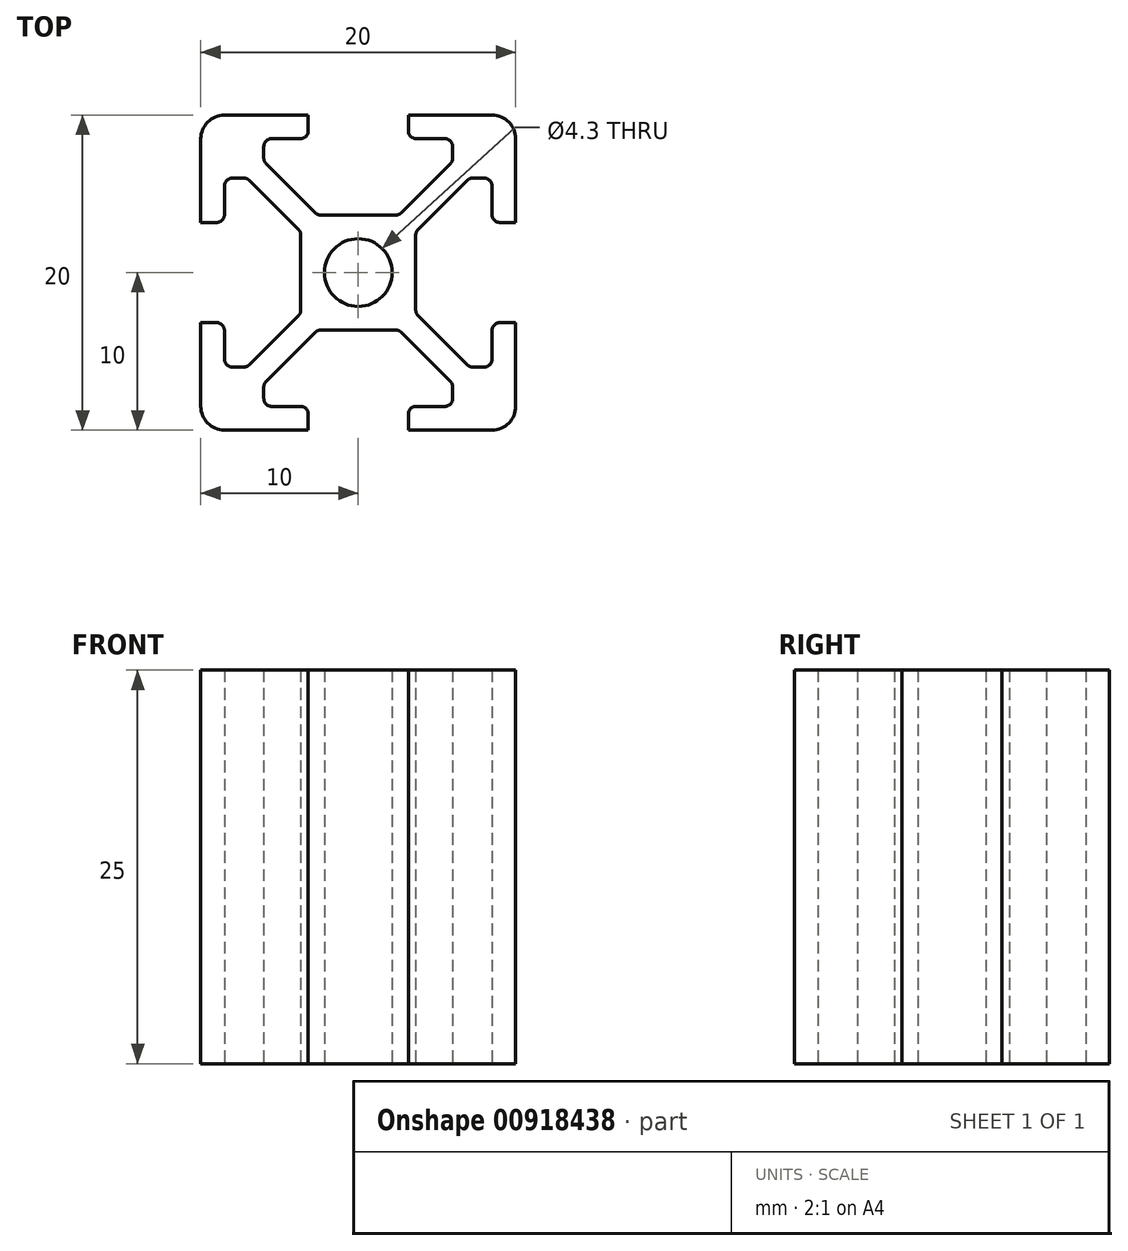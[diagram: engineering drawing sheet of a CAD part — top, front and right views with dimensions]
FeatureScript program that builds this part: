
annotation { "Feature Type Name" : "Feature", "Feature Type Description" : "" }
export const myFeature = defineFeature(function(context is Context, id is Id, definition is map)
    precondition{}
    {
        {
            var Q0;
            Q0=qCreatedBy(makeId("Top.planeOp"),FACE);
            var sketch = newSketch(context, id + "F0", { "sketchPlane" : qUnion([Q0])});
            skPoint(sketch, "E0.middle", {"position": v(0, 0) * mm});
            skCircle(sketch, "E1", {"center": v(0, 0) * mm, "radius": 2.15 * mm});
            skLineSegment(sketch, "E2.bottom", {"start": v(10, 10) * mm, "end": v(-10, 10) * mm});
            skLineSegment(sketch, "E2.top", {"start": v(10, -10) * mm, "end": v(-10, -10) * mm});
            skLineSegment(sketch, "E2.left", {"start": v(10, 10) * mm, "end": v(10, -10) * mm});
            skLineSegment(sketch, "E2.right", {"start": v(-10, 10) * mm, "end": v(-10, -10) * mm});
            skSolve(sketch);
        }
        {
            var Q0;
            Q0=makeQuery(id+"F0.imprint","IMPRINT",FACE,{"disambiguationData":[TD([[makeQuery(id+"F0.imprint","IMPRINT",EDGE,{"derivedFrom":sQuery(id+"F0.wireOp",EDGE,"E1")}),-1.0]])]});
            var sketch = newSketch(context, id + "F1", { "sketchPlane" : qUnion([Q0])});
            skLineSegment(sketch, "E3", {"start": v(-3.18, 10) * mm, "end": v(3.18, 10) * mm});
            skLineSegment(sketch, "E4", {"start": v(3.18, 10) * mm, "end": v(3.18, 8.5) * mm});
            skLineSegment(sketch, "E5", {"start": v(3.18, 8.5) * mm, "end": v(6, 8.5) * mm});
            skLineSegment(sketch, "E6", {"start": v(6, 8.5) * mm, "end": v(6, 7.06) * mm});
            skLineSegment(sketch, "E7", {"start": v(6, 7.06) * mm, "end": v(2.59, 3.65) * mm});
            skLineSegment(sketch, "E8", {"start": v(2.59, 3.65) * mm, "end": v(-2.59, 3.65) * mm});
            skLineSegment(sketch, "E9", {"start": v(-2.59, 3.65) * mm, "end": v(-6, 7.06) * mm});
            skLineSegment(sketch, "E10", {"start": v(-6, 7.06) * mm, "end": v(-6, 8.5) * mm});
            skLineSegment(sketch, "E11", {"start": v(-6, 8.5) * mm, "end": v(-3.18, 8.5) * mm});
            skLineSegment(sketch, "E12", {"start": v(-3.18, 8.5) * mm, "end": v(-3.18, 10) * mm});
            skPoint(sketch, "E13", {"position": v(0, 10) * mm});
            skPoint(sketch, "E14", {"position": v(0, 3.65) * mm});
            skPoint(sketch, "E15.center", {"position": v(0.01, -0.04) * mm});
            skLineSegment(sketch, "E16.0.0", {"start": v(-10, -10) * mm, "end": v(10, -10) * mm});
            skLineSegment(sketch, "E16.0.1", {"start": v(10, -10) * mm, "end": v(10, 10) * mm});
            skLineSegment(sketch, "E16.0.2", {"start": v(10, 10) * mm, "end": v(-10, 10) * mm});
            skLineSegment(sketch, "E16.0.3", {"start": v(-10, 10) * mm, "end": v(-10, -10) * mm});
            skLineSegment(sketch, "E17", {"start": v(0, 0) * mm, "end": v(10, 10) * mm, "construction": true});
            skLineSegment(sketch, "E18.1.0", {"start": v(-8.5, -3.18) * mm, "end": v(-10, -3.18) * mm});
            skLineSegment(sketch, "E18.1.1", {"start": v(-8.5, -6) * mm, "end": v(-8.5, -3.18) * mm});
            skLineSegment(sketch, "E18.1.2", {"start": v(-7.06, -6) * mm, "end": v(-8.5, -6) * mm});
            skLineSegment(sketch, "E18.1.3", {"start": v(-3.65, -2.59) * mm, "end": v(-7.06, -6) * mm});
            skLineSegment(sketch, "E18.1.4", {"start": v(-3.65, 2.59) * mm, "end": v(-3.65, -2.59) * mm});
            skLineSegment(sketch, "E18.1.5", {"start": v(-7.06, 6) * mm, "end": v(-3.65, 2.59) * mm});
            skLineSegment(sketch, "E18.1.6", {"start": v(-8.5, 6) * mm, "end": v(-7.06, 6) * mm});
            skLineSegment(sketch, "E18.1.7", {"start": v(-8.5, 3.18) * mm, "end": v(-8.5, 6) * mm});
            skLineSegment(sketch, "E18.1.8", {"start": v(-10, 3.18) * mm, "end": v(-8.5, 3.18) * mm});
            skLineSegment(sketch, "E18.2.0", {"start": v(3.18, -8.5) * mm, "end": v(3.18, -10) * mm});
            skLineSegment(sketch, "E18.2.1", {"start": v(6, -8.5) * mm, "end": v(3.18, -8.5) * mm});
            skLineSegment(sketch, "E18.2.2", {"start": v(6, -7.06) * mm, "end": v(6, -8.5) * mm});
            skLineSegment(sketch, "E18.2.3", {"start": v(2.59, -3.65) * mm, "end": v(6, -7.06) * mm});
            skLineSegment(sketch, "E18.2.4", {"start": v(-2.59, -3.65) * mm, "end": v(2.59, -3.65) * mm});
            skLineSegment(sketch, "E18.2.5", {"start": v(-6, -7.06) * mm, "end": v(-2.59, -3.65) * mm});
            skLineSegment(sketch, "E18.2.6", {"start": v(-6, -8.5) * mm, "end": v(-6, -7.06) * mm});
            skLineSegment(sketch, "E18.2.7", {"start": v(-3.18, -8.5) * mm, "end": v(-6, -8.5) * mm});
            skLineSegment(sketch, "E18.2.8", {"start": v(-3.18, -10) * mm, "end": v(-3.18, -8.5) * mm});
            skLineSegment(sketch, "E18.3.0", {"start": v(8.5, 3.18) * mm, "end": v(10, 3.18) * mm});
            skLineSegment(sketch, "E18.3.1", {"start": v(8.5, 6) * mm, "end": v(8.5, 3.18) * mm});
            skLineSegment(sketch, "E18.3.2", {"start": v(7.06, 6) * mm, "end": v(8.5, 6) * mm});
            skLineSegment(sketch, "E18.3.3", {"start": v(3.65, 2.59) * mm, "end": v(7.06, 6) * mm});
            skLineSegment(sketch, "E18.3.4", {"start": v(3.65, -2.59) * mm, "end": v(3.65, 2.59) * mm});
            skLineSegment(sketch, "E18.3.5", {"start": v(7.06, -6) * mm, "end": v(3.65, -2.59) * mm});
            skLineSegment(sketch, "E18.3.6", {"start": v(8.5, -6) * mm, "end": v(7.06, -6) * mm});
            skLineSegment(sketch, "E18.3.7", {"start": v(8.5, -3.18) * mm, "end": v(8.5, -6) * mm});
            skLineSegment(sketch, "E18.3.8", {"start": v(10, -3.18) * mm, "end": v(8.5, -3.18) * mm});
            skPoint(sketch, "E18.center", {"position": v(0, 0) * mm});
            skSolve(sketch);
        }
        {
            var Q0;
            Q0=makeQuery(id+"F0.imprint","IMPRINT",FACE,{"disambiguationData":[TD([[makeQuery(id+"F0.imprint","IMPRINT",EDGE,{"derivedFrom":sQuery(id+"F0.wireOp",EDGE,"E1")}),-1.0]])]});
            extrude(context, id + "F2", {"entities" : qUnion([Q0]), "flatOperationType" : FlatOperationType.REMOVE, "depth" : 25 * mm, "offsetDistance" : 25 * mm, "domain" : OperationDomain.MODEL});
        }
        {
            var Q0;
            {var subQ0=sQuery(id+"F1.wireOp",EDGE,"E18.1.0");Q0=makeQuery(id+"F1.imprint","IMPRINT",FACE,{"disambiguationData":[TD([[makeQuery(id+"F1.imprint","IMPRINT",EDGE,{"derivedFrom":subQ0}),-1.0]])]});}
            var Q1;
            {var subQ0=sQuery(id+"F1.wireOp",EDGE,"E18.2.0");Q1=makeQuery(id+"F1.imprint","IMPRINT",FACE,{"disambiguationData":[TD([[makeQuery(id+"F1.imprint","IMPRINT",EDGE,{"derivedFrom":subQ0}),-1.0]])]});}
            var Q2;
            {var subQ0=sQuery(id+"F1.wireOp",EDGE,"E18.3.0");Q2=makeQuery(id+"F1.imprint","IMPRINT",FACE,{"disambiguationData":[TD([[makeQuery(id+"F1.imprint","IMPRINT",EDGE,{"derivedFrom":subQ0}),-1.0]])]});}
            var Q3;
            {var subQ0=sQuery(id+"F1.wireOp",EDGE,"E4");Q3=makeQuery(id+"F1.imprint","IMPRINT",FACE,{"disambiguationData":[TD([[makeQuery(id+"F1.imprint","IMPRINT",EDGE,{"derivedFrom":subQ0}),-1.0]])]});}
            extrude(context, id + "F3", {"entities" : qUnion([Q0, Q1, Q2, Q3]), "operationType" : NewBodyOperationType.REMOVE, "endBound" : BoundingType.THROUGH_ALL, "depth" : 25 * mm, "offsetDistance" : 25 * mm});
        }
        {
            var Q0;
            Q0=makeQuery(id+"F2.opExtrude","SWEPT_EDGE",EDGE,{"disambiguationData":[OSD([sQuery(id+"F0.wireOp",EDGE,"E2.top"),sQuery(id+"F0.wireOp",EDGE,"E2.left")])]});
            var Q1;
            Q1=makeQuery(id+"F2.opExtrude","SWEPT_EDGE",EDGE,{"disambiguationData":[OSD([sQuery(id+"F0.wireOp",EDGE,"E2.top"),sQuery(id+"F0.wireOp",EDGE,"E2.right")])]});
            var Q2;
            Q2=makeQuery(id+"F2.opExtrude","SWEPT_EDGE",EDGE,{"disambiguationData":[OSD([sQuery(id+"F0.wireOp",EDGE,"E2.bottom"),sQuery(id+"F0.wireOp",EDGE,"E2.left")])]});
            var Q3;
            Q3=makeQuery(id+"F2.opExtrude","SWEPT_EDGE",EDGE,{"disambiguationData":[OSD([sQuery(id+"F0.wireOp",EDGE,"E2.bottom"),sQuery(id+"F0.wireOp",EDGE,"E2.right")])]});
            fillet(context, id + "F4", {"entities" : qUnion([Q0, Q1, Q2, Q3]), "radius" : 1.5 * mm, "tangentPropagation" : true, "allowEdgeOverflow" : false});
        }
        {
            var Q0;
            Q0=makeQuery(id+"F3.boolean.opBoolean","COPY",EDGE,{"derivedFrom":makeQuery(id+"F3.opExtrude","SWEPT_EDGE",EDGE,{"disambiguationData":[OSD([sQuery(id+"F1.wireOp",EDGE,"E16.0.0"),sQuery(id+"F1.wireOp",EDGE,"E18.2.8")])]})});
            var Q1;
            Q1=makeQuery(id+"F3.boolean.opBoolean","COPY",EDGE,{"derivedFrom":makeQuery(id+"F3.opExtrude","SWEPT_EDGE",EDGE,{"disambiguationData":[OSD([sQuery(id+"F1.wireOp",EDGE,"E16.0.3"),sQuery(id+"F1.wireOp",EDGE,"E18.1.8")])]})});
            var Q2;
            Q2=makeQuery(id+"F3.boolean.opBoolean","COPY",EDGE,{"derivedFrom":makeQuery(id+"F3.opExtrude","SWEPT_EDGE",EDGE,{"disambiguationData":[OSD([sQuery(id+"F1.wireOp",EDGE,"E12"),sQuery(id+"F1.wireOp",EDGE,"E16.0.2")])]})});
            var Q3;
            Q3=makeQuery(id+"F3.boolean.opBoolean","COPY",EDGE,{"derivedFrom":makeQuery(id+"F3.opExtrude","SWEPT_EDGE",EDGE,{"disambiguationData":[OSD([sQuery(id+"F1.wireOp",EDGE,"E16.0.0"),sQuery(id+"F1.wireOp",EDGE,"E18.2.0")])]})});
            var Q4;
            Q4=makeQuery(id+"F3.boolean.opBoolean","COPY",EDGE,{"derivedFrom":makeQuery(id+"F3.opExtrude","SWEPT_EDGE",EDGE,{"disambiguationData":[OSD([sQuery(id+"F1.wireOp",EDGE,"E16.0.1"),sQuery(id+"F1.wireOp",EDGE,"E18.3.0")])]})});
            var Q5;
            Q5=makeQuery(id+"F3.boolean.opBoolean","COPY",EDGE,{"derivedFrom":makeQuery(id+"F3.opExtrude","SWEPT_EDGE",EDGE,{"disambiguationData":[OSD([sQuery(id+"F1.wireOp",EDGE,"E16.0.1"),sQuery(id+"F1.wireOp",EDGE,"E18.3.8")])]})});
            var Q6;
            Q6=makeQuery(id+"F3.boolean.opBoolean","COPY",EDGE,{"derivedFrom":makeQuery(id+"F3.opExtrude","SWEPT_EDGE",EDGE,{"disambiguationData":[OSD([sQuery(id+"F1.wireOp",EDGE,"E16.0.3"),sQuery(id+"F1.wireOp",EDGE,"E18.1.0")])]})});
            var Q7;
            Q7=makeQuery(id+"F3.boolean.opBoolean","COPY",EDGE,{"derivedFrom":makeQuery(id+"F3.opExtrude","SWEPT_EDGE",EDGE,{"disambiguationData":[OSD([sQuery(id+"F1.wireOp",EDGE,"E4"),sQuery(id+"F1.wireOp",EDGE,"E16.0.2")])]})});
            var Q8;
            Q8=makeQuery(id+"F3.boolean.opBoolean","COPY",EDGE,{"derivedFrom":makeQuery(id+"F3.opExtrude","SWEPT_EDGE",EDGE,{"disambiguationData":[OSD([sQuery(id+"F1.wireOp",EDGE,"E18.2.6"),sQuery(id+"F1.wireOp",EDGE,"E18.2.7")])]})});
            var Q9;
            Q9=makeQuery(id+"F3.boolean.opBoolean","COPY",EDGE,{"derivedFrom":makeQuery(id+"F3.opExtrude","SWEPT_EDGE",EDGE,{"disambiguationData":[OSD([sQuery(id+"F1.wireOp",EDGE,"E18.2.7"),sQuery(id+"F1.wireOp",EDGE,"E18.2.8")])]})});
            var Q10;
            Q10=makeQuery(id+"F3.boolean.opBoolean","COPY",EDGE,{"derivedFrom":makeQuery(id+"F3.opExtrude","SWEPT_EDGE",EDGE,{"disambiguationData":[OSD([sQuery(id+"F1.wireOp",EDGE,"E18.2.0"),sQuery(id+"F1.wireOp",EDGE,"E18.2.1")])]})});
            var Q11;
            Q11=makeQuery(id+"F3.boolean.opBoolean","COPY",EDGE,{"derivedFrom":makeQuery(id+"F3.opExtrude","SWEPT_EDGE",EDGE,{"disambiguationData":[OSD([sQuery(id+"F1.wireOp",EDGE,"E18.1.7"),sQuery(id+"F1.wireOp",EDGE,"E18.1.8")])]})});
            var Q12;
            Q12=makeQuery(id+"F3.boolean.opBoolean","COPY",EDGE,{"derivedFrom":makeQuery(id+"F3.opExtrude","SWEPT_EDGE",EDGE,{"disambiguationData":[OSD([sQuery(id+"F1.wireOp",EDGE,"E18.1.0"),sQuery(id+"F1.wireOp",EDGE,"E18.1.1")])]})});
            var Q13;
            Q13=makeQuery(id+"F3.boolean.opBoolean","COPY",EDGE,{"derivedFrom":makeQuery(id+"F3.opExtrude","SWEPT_EDGE",EDGE,{"disambiguationData":[OSD([sQuery(id+"F1.wireOp",EDGE,"E18.3.7"),sQuery(id+"F1.wireOp",EDGE,"E18.3.8")])]})});
            var Q14;
            Q14=makeQuery(id+"F3.boolean.opBoolean","COPY",EDGE,{"derivedFrom":makeQuery(id+"F3.opExtrude","SWEPT_EDGE",EDGE,{"disambiguationData":[OSD([sQuery(id+"F1.wireOp",EDGE,"E18.3.0"),sQuery(id+"F1.wireOp",EDGE,"E18.3.1")])]})});
            var Q15;
            Q15=makeQuery(id+"F3.boolean.opBoolean","COPY",EDGE,{"derivedFrom":makeQuery(id+"F3.opExtrude","SWEPT_EDGE",EDGE,{"disambiguationData":[OSD([sQuery(id+"F1.wireOp",EDGE,"E4"),sQuery(id+"F1.wireOp",EDGE,"E5")])]})});
            var Q16;
            Q16=makeQuery(id+"F3.boolean.opBoolean","COPY",EDGE,{"derivedFrom":makeQuery(id+"F3.opExtrude","SWEPT_EDGE",EDGE,{"disambiguationData":[OSD([sQuery(id+"F1.wireOp",EDGE,"E5"),sQuery(id+"F1.wireOp",EDGE,"E6")])]})});
            var Q17;
            Q17=makeQuery(id+"F3.boolean.opBoolean","COPY",EDGE,{"derivedFrom":makeQuery(id+"F3.opExtrude","SWEPT_EDGE",EDGE,{"disambiguationData":[OSD([sQuery(id+"F1.wireOp",EDGE,"E18.3.1"),sQuery(id+"F1.wireOp",EDGE,"E18.3.2")])]})});
            var Q18;
            Q18=makeQuery(id+"F3.boolean.opBoolean","COPY",EDGE,{"derivedFrom":makeQuery(id+"F3.opExtrude","SWEPT_EDGE",EDGE,{"disambiguationData":[OSD([sQuery(id+"F1.wireOp",EDGE,"E18.3.2"),sQuery(id+"F1.wireOp",EDGE,"E18.3.3")])]})});
            var Q19;
            Q19=makeQuery(id+"F3.boolean.opBoolean","COPY",EDGE,{"derivedFrom":makeQuery(id+"F3.opExtrude","SWEPT_EDGE",EDGE,{"disambiguationData":[OSD([sQuery(id+"F1.wireOp",EDGE,"E6"),sQuery(id+"F1.wireOp",EDGE,"E7")])]})});
            var Q20;
            Q20=makeQuery(id+"F3.boolean.opBoolean","COPY",EDGE,{"derivedFrom":makeQuery(id+"F3.opExtrude","SWEPT_EDGE",EDGE,{"disambiguationData":[OSD([sQuery(id+"F1.wireOp",EDGE,"E18.2.4"),sQuery(id+"F1.wireOp",EDGE,"E18.2.5")])]})});
            var Q21;
            Q21=makeQuery(id+"F3.boolean.opBoolean","COPY",EDGE,{"derivedFrom":makeQuery(id+"F3.opExtrude","SWEPT_EDGE",EDGE,{"disambiguationData":[OSD([sQuery(id+"F1.wireOp",EDGE,"E18.2.3"),sQuery(id+"F1.wireOp",EDGE,"E18.2.4")])]})});
            var Q22;
            Q22=makeQuery(id+"F3.boolean.opBoolean","COPY",EDGE,{"derivedFrom":makeQuery(id+"F3.opExtrude","SWEPT_EDGE",EDGE,{"disambiguationData":[OSD([sQuery(id+"F1.wireOp",EDGE,"E18.3.3"),sQuery(id+"F1.wireOp",EDGE,"E18.3.4")])]})});
            var Q23;
            Q23=makeQuery(id+"F3.boolean.opBoolean","COPY",EDGE,{"derivedFrom":makeQuery(id+"F3.opExtrude","SWEPT_EDGE",EDGE,{"disambiguationData":[OSD([sQuery(id+"F1.wireOp",EDGE,"E18.3.4"),sQuery(id+"F1.wireOp",EDGE,"E18.3.5")])]})});
            var Q24;
            Q24=makeQuery(id+"F3.boolean.opBoolean","COPY",EDGE,{"derivedFrom":makeQuery(id+"F3.opExtrude","SWEPT_EDGE",EDGE,{"disambiguationData":[OSD([sQuery(id+"F1.wireOp",EDGE,"E18.1.3"),sQuery(id+"F1.wireOp",EDGE,"E18.1.4")])]})});
            var Q25;
            Q25=makeQuery(id+"F3.boolean.opBoolean","COPY",EDGE,{"derivedFrom":makeQuery(id+"F3.opExtrude","SWEPT_EDGE",EDGE,{"disambiguationData":[OSD([sQuery(id+"F1.wireOp",EDGE,"E18.1.4"),sQuery(id+"F1.wireOp",EDGE,"E18.1.5")])]})});
            var Q26;
            Q26=makeQuery(id+"F3.boolean.opBoolean","COPY",EDGE,{"derivedFrom":makeQuery(id+"F3.opExtrude","SWEPT_EDGE",EDGE,{"disambiguationData":[OSD([sQuery(id+"F1.wireOp",EDGE,"E7"),sQuery(id+"F1.wireOp",EDGE,"E8")])]})});
            var Q27;
            Q27=makeQuery(id+"F3.boolean.opBoolean","COPY",EDGE,{"derivedFrom":makeQuery(id+"F3.opExtrude","SWEPT_EDGE",EDGE,{"disambiguationData":[OSD([sQuery(id+"F1.wireOp",EDGE,"E8"),sQuery(id+"F1.wireOp",EDGE,"E9")])]})});
            var Q28;
            Q28=makeQuery(id+"F3.boolean.opBoolean","COPY",EDGE,{"derivedFrom":makeQuery(id+"F3.opExtrude","SWEPT_EDGE",EDGE,{"disambiguationData":[OSD([sQuery(id+"F1.wireOp",EDGE,"E10"),sQuery(id+"F1.wireOp",EDGE,"E11")])]})});
            var Q29;
            Q29=makeQuery(id+"F3.boolean.opBoolean","COPY",EDGE,{"derivedFrom":makeQuery(id+"F3.opExtrude","SWEPT_EDGE",EDGE,{"disambiguationData":[OSD([sQuery(id+"F1.wireOp",EDGE,"E9"),sQuery(id+"F1.wireOp",EDGE,"E10")])]})});
            var Q30;
            Q30=makeQuery(id+"F3.boolean.opBoolean","COPY",EDGE,{"derivedFrom":makeQuery(id+"F3.opExtrude","SWEPT_EDGE",EDGE,{"disambiguationData":[OSD([sQuery(id+"F1.wireOp",EDGE,"E11"),sQuery(id+"F1.wireOp",EDGE,"E12")])]})});
            var Q31;
            Q31=makeQuery(id+"F3.boolean.opBoolean","COPY",EDGE,{"derivedFrom":makeQuery(id+"F3.opExtrude","SWEPT_EDGE",EDGE,{"disambiguationData":[OSD([sQuery(id+"F1.wireOp",EDGE,"E18.3.6"),sQuery(id+"F1.wireOp",EDGE,"E18.3.7")])]})});
            var Q32;
            Q32=makeQuery(id+"F3.boolean.opBoolean","COPY",EDGE,{"derivedFrom":makeQuery(id+"F3.opExtrude","SWEPT_EDGE",EDGE,{"disambiguationData":[OSD([sQuery(id+"F1.wireOp",EDGE,"E18.3.5"),sQuery(id+"F1.wireOp",EDGE,"E18.3.6")])]})});
            var Q33;
            Q33=makeQuery(id+"F3.boolean.opBoolean","COPY",EDGE,{"derivedFrom":makeQuery(id+"F3.opExtrude","SWEPT_EDGE",EDGE,{"disambiguationData":[OSD([sQuery(id+"F1.wireOp",EDGE,"E18.1.1"),sQuery(id+"F1.wireOp",EDGE,"E18.1.2")])]})});
            var Q34;
            Q34=makeQuery(id+"F3.boolean.opBoolean","COPY",EDGE,{"derivedFrom":makeQuery(id+"F3.opExtrude","SWEPT_EDGE",EDGE,{"disambiguationData":[OSD([sQuery(id+"F1.wireOp",EDGE,"E18.1.2"),sQuery(id+"F1.wireOp",EDGE,"E18.1.3")])]})});
            var Q35;
            Q35=makeQuery(id+"F3.boolean.opBoolean","COPY",EDGE,{"derivedFrom":makeQuery(id+"F3.opExtrude","SWEPT_EDGE",EDGE,{"disambiguationData":[OSD([sQuery(id+"F1.wireOp",EDGE,"E18.2.5"),sQuery(id+"F1.wireOp",EDGE,"E18.2.6")])]})});
            var Q36;
            Q36=makeQuery(id+"F3.boolean.opBoolean","COPY",EDGE,{"derivedFrom":makeQuery(id+"F3.opExtrude","SWEPT_EDGE",EDGE,{"disambiguationData":[OSD([sQuery(id+"F1.wireOp",EDGE,"E18.2.2"),sQuery(id+"F1.wireOp",EDGE,"E18.2.3")])]})});
            var Q37;
            Q37=makeQuery(id+"F3.boolean.opBoolean","COPY",EDGE,{"derivedFrom":makeQuery(id+"F3.opExtrude","SWEPT_EDGE",EDGE,{"disambiguationData":[OSD([sQuery(id+"F1.wireOp",EDGE,"E18.2.1"),sQuery(id+"F1.wireOp",EDGE,"E18.2.2")])]})});
            var Q38;
            Q38=makeQuery(id+"F3.boolean.opBoolean","COPY",EDGE,{"derivedFrom":makeQuery(id+"F3.opExtrude","SWEPT_EDGE",EDGE,{"disambiguationData":[OSD([sQuery(id+"F1.wireOp",EDGE,"E18.1.6"),sQuery(id+"F1.wireOp",EDGE,"E18.1.7")])]})});
            var Q39;
            Q39=makeQuery(id+"F3.boolean.opBoolean","COPY",EDGE,{"derivedFrom":makeQuery(id+"F3.opExtrude","SWEPT_EDGE",EDGE,{"disambiguationData":[OSD([sQuery(id+"F1.wireOp",EDGE,"E18.1.5"),sQuery(id+"F1.wireOp",EDGE,"E18.1.6")])]})});
            fillet(context, id + "F5", {"entities" : qUnion([Q0, Q1, Q2, Q3, Q4, Q5, Q6, Q7, Q8, Q9, Q10, Q11, Q12, Q13, Q14, Q15, Q16, Q17, Q18, Q19, Q20, Q21, Q22, Q23, Q24, Q25, Q26, Q27, Q28, Q29, Q30, Q31, Q32, Q33, Q34, Q35, Q36, Q37, Q38, Q39]), "radius" : 0.5 * mm, "tangentPropagation" : true, "allowEdgeOverflow" : false});
        }
    });
